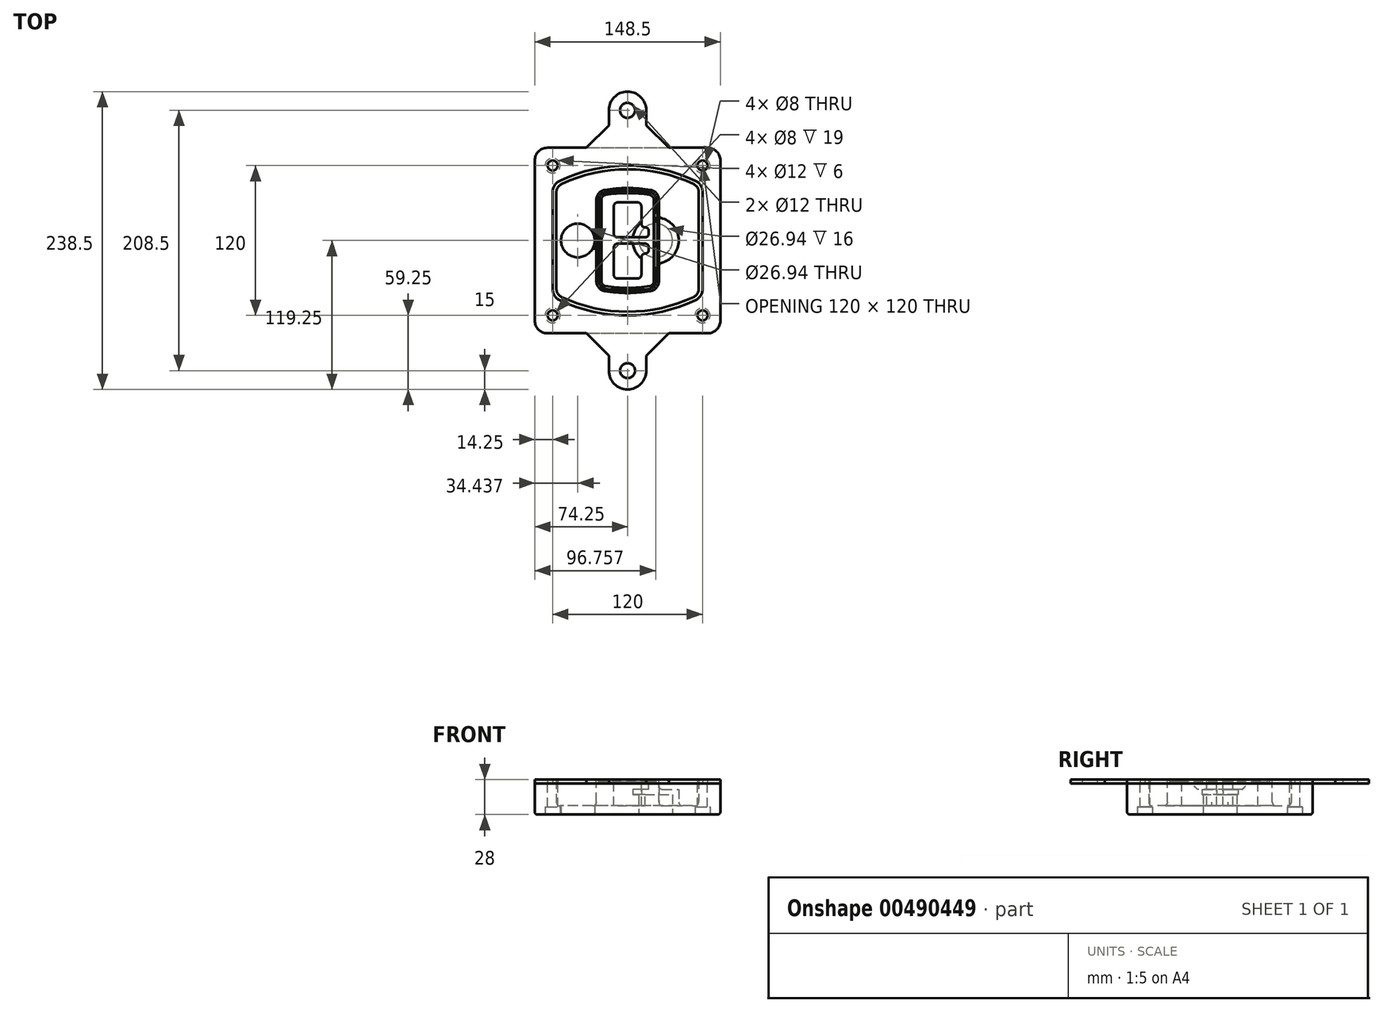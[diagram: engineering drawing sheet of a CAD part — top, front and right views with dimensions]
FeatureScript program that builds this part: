
annotation { "Feature Type Name" : "Feature", "Feature Type Description" : "" }
export const myFeature = defineFeature(function(context is Context, id is Id, definition is map)
    precondition{}
    {
        {
            var Q0;
            Q0=qCreatedBy(makeId("Top.planeOp"),FACE);
            var sketch = newSketch(context, id + "F0", { "sketchPlane" : qUnion([Q0])});
            skPoint(sketch, "E0.rect.middle", {"position": v(0, 0) * mm});
            skLineSegment(sketch, "E1.bottom", {"start": v(-64.25, -74.25) * mm, "end": v(64.25, -74.25) * mm});
            skLineSegment(sketch, "E1.top", {"start": v(-64.25, 74.25) * mm, "end": v(64.25, 74.25) * mm});
            skLineSegment(sketch, "E1.left", {"start": v(-74.25, -64.25) * mm, "end": v(-74.25, 64.25) * mm});
            skLineSegment(sketch, "E1.right", {"start": v(74.25, -64.25) * mm, "end": v(74.25, 64.25) * mm});
            skLineSegment(sketch, "E2", {"start": v(-74.25, 74.25) * mm, "end": v(74.25, -74.25) * mm, "construction": true});
            skLineSegment(sketch, "E3", {"start": v(74.25, 74.25) * mm, "end": v(-74.25, -74.25) * mm, "construction": true});
            skCircle(sketch, "E4", {"center": v(-60, 60) * mm, "radius": 4 * mm});
            skCircle(sketch, "E5", {"center": v(60, 60) * mm, "radius": 4 * mm});
            skCircle(sketch, "E6", {"center": v(60, -60) * mm, "radius": 4 * mm});
            skCircle(sketch, "E7", {"center": v(-60, -60) * mm, "radius": 4 * mm});
            skLineSegment(sketch, "E8", {"start": v(-60, 60) * mm, "end": v(60, 60) * mm, "construction": true});
            skLineSegment(sketch, "E9", {"start": v(60, 60) * mm, "end": v(60, -60) * mm, "construction": true});
            skLineSegment(sketch, "E10", {"start": v(60, -60) * mm, "end": v(-60, -60) * mm, "construction": true});
            skLineSegment(sketch, "E11", {"start": v(-60, -60) * mm, "end": v(-60, 60) * mm, "construction": true});
            skLineSegment(sketch, "E12", {"start": v(-60, 38.83) * mm, "end": v(-60, -38.83) * mm});
            skLineSegment(sketch, "E13", {"start": v(60, 38.83) * mm, "end": v(60, -38.83) * mm});
            skArc(sketch, "E14", {"start": v(54.26, 47.88) * mm, "mid": v(0, 60) * mm, "end": v(-54.26, 47.88) * mm});
            skArc(sketch, "E15", {"start": v(-54.26, -47.88) * mm, "mid": v(0, -60) * mm, "end": v(54.26, -47.88) * mm});
            skLineSegment(sketch, "E16", {"start": v(-60, 0) * mm, "end": v(60, 0) * mm, "construction": true});
            skPoint(sketch, "E17.visualSharp", {"position": v(-60, -45) * mm});
            skArc(sketch, "E17.filletArc", {"start": v(-60, -38.83) * mm, "mid": v(-58.44, -44.2) * mm, "end": v(-54.26, -47.88) * mm});
            skPoint(sketch, "E18.visualSharp", {"position": v(-60, 45) * mm});
            skArc(sketch, "E18.filletArc", {"start": v(-54.26, 47.88) * mm, "mid": v(-58.44, 44.2) * mm, "end": v(-60, 38.83) * mm});
            skPoint(sketch, "E19.visualSharp", {"position": v(60, 45) * mm});
            skArc(sketch, "E19.filletArc", {"start": v(60, 38.83) * mm, "mid": v(58.44, 44.2) * mm, "end": v(54.26, 47.88) * mm});
            skPoint(sketch, "E20.visualSharp", {"position": v(60, -45) * mm});
            skArc(sketch, "E20.filletArc", {"start": v(54.26, -47.88) * mm, "mid": v(58.44, -44.2) * mm, "end": v(60, -38.83) * mm});
            skPoint(sketch, "E21.visualSharp", {"position": v(-74.25, 74.25) * mm});
            skArc(sketch, "E21.filletArc", {"start": v(-64.25, 74.25) * mm, "mid": v(-71.32, 71.32) * mm, "end": v(-74.25, 64.25) * mm});
            skPoint(sketch, "E22.visualSharp", {"position": v(74.25, 74.25) * mm});
            skArc(sketch, "E22.filletArc", {"start": v(74.25, 64.25) * mm, "mid": v(71.32, 71.32) * mm, "end": v(64.25, 74.25) * mm});
            skPoint(sketch, "E23.visualSharp", {"position": v(74.25, -74.25) * mm});
            skArc(sketch, "E23.filletArc", {"start": v(64.25, -74.25) * mm, "mid": v(71.32, -71.32) * mm, "end": v(74.25, -64.25) * mm});
            skPoint(sketch, "E24.visualSharp", {"position": v(-74.25, -74.25) * mm});
            skArc(sketch, "E24.filletArc", {"start": v(-74.25, -64.25) * mm, "mid": v(-71.32, -71.32) * mm, "end": v(-64.25, -74.25) * mm});
            skArc(sketch, "E25.0", {"start": v(57, 38.83) * mm, "mid": v(55.9, 42.58) * mm, "end": v(52.98, 45.17) * mm});
            skLineSegment(sketch, "E25.1", {"start": v(57, 38.83) * mm, "end": v(57, -38.83) * mm});
            skArc(sketch, "E25.2", {"start": v(52.98, -45.17) * mm, "mid": v(55.9, -42.58) * mm, "end": v(57, -38.83) * mm});
            skArc(sketch, "E25.3", {"start": v(-52.98, -45.17) * mm, "mid": v(0, -57) * mm, "end": v(52.98, -45.17) * mm});
            skArc(sketch, "E25.4", {"start": v(-57, -38.83) * mm, "mid": v(-55.9, -42.58) * mm, "end": v(-52.98, -45.17) * mm});
            skArc(sketch, "E25.5", {"start": v(52.98, 45.17) * mm, "mid": v(0, 57) * mm, "end": v(-52.98, 45.17) * mm});
            skLineSegment(sketch, "E25.6", {"start": v(-57, 38.83) * mm, "end": v(-57, -38.83) * mm});
            skArc(sketch, "E25.7", {"start": v(-52.98, 45.17) * mm, "mid": v(-55.9, 42.58) * mm, "end": v(-57, 38.83) * mm});
            skArc(sketch, "E26.0", {"start": v(-55.96, 51.5) * mm, "mid": v(-61.82, 46.33) * mm, "end": v(-64, 38.83) * mm});
            skArc(sketch, "E26.1", {"start": v(55.96, 51.5) * mm, "mid": v(0, 64) * mm, "end": v(-55.96, 51.5) * mm});
            skArc(sketch, "E26.2", {"start": v(64, 38.83) * mm, "mid": v(61.82, 46.33) * mm, "end": v(55.96, 51.5) * mm});
            skLineSegment(sketch, "E26.3", {"start": v(64, 38.83) * mm, "end": v(64, -38.83) * mm});
            skArc(sketch, "E26.4", {"start": v(55.96, -51.5) * mm, "mid": v(61.82, -46.33) * mm, "end": v(64, -38.83) * mm});
            skLineSegment(sketch, "E26.5", {"start": v(-64, 38.83) * mm, "end": v(-64, -38.83) * mm});
            skArc(sketch, "E26.6", {"start": v(-55.96, -51.5) * mm, "mid": v(0, -64) * mm, "end": v(55.96, -51.5) * mm});
            skArc(sketch, "E26.7", {"start": v(-64, -38.83) * mm, "mid": v(-61.82, -46.33) * mm, "end": v(-55.96, -51.5) * mm});
            skSolve(sketch);
        }
        {
            var Q0;
            Q0=makeQuery(id+"F0.imprint","IMPRINT",FACE,{"disambiguationData":[TD([[makeQuery(id+"F0.imprint","IMPRINT",EDGE,{"derivedFrom":sQuery(id+"F0.wireOp",EDGE,"E1.bottom")}),1.0]])]});
            var Q1;
            Q1=makeQuery(id+"F0.imprint","IMPRINT",FACE,{"disambiguationData":[TD([[makeQuery(id+"F0.imprint","IMPRINT",EDGE,{"derivedFrom":sQuery(id+"F0.wireOp",EDGE,"E12")}),1.0]])]});
            var Q2;
            Q2=makeQuery(id+"F0.imprint","IMPRINT",FACE,{"disambiguationData":[TD([[makeQuery(id+"F0.imprint","IMPRINT",EDGE,{"derivedFrom":sQuery(id+"F0.wireOp",EDGE,"E25.0")}),1.0]])]});
            var Q3;
            Q3=makeQuery(id+"F0.imprint","IMPRINT",FACE,{"disambiguationData":[TD([[makeQuery(id+"F0.imprint","IMPRINT",EDGE,{"derivedFrom":sQuery(id+"F0.wireOp",EDGE,"E12")}),-1.0]])]});
            extrude(context, id + "F1", {"entities" : qUnion([Q0, Q1, Q2, Q3]), "oppositeDirection" : true, "depth" : 25 * mm});
        }
        {
            var Q0;
            Q0=makeQuery(id+"F0.imprint","IMPRINT",FACE,{"disambiguationData":[TD([[makeQuery(id+"F0.imprint","IMPRINT",EDGE,{"derivedFrom":sQuery(id+"F0.wireOp",EDGE,"E12")}),1.0]])]});
            extrude(context, id + "F2", {"entities" : qUnion([Q0]), "operationType" : NewBodyOperationType.ADD, "depth" : 3 * mm});
        }
        {
            var Q0;
            Q0=makeQuery(id+"F0.imprint","IMPRINT",FACE,{"disambiguationData":[TD([[makeQuery(id+"F0.imprint","IMPRINT",EDGE,{"derivedFrom":sQuery(id+"F0.wireOp",EDGE,"E25.0")}),1.0]])]});
            extrude(context, id + "F3", {"entities" : qUnion([Q0]), "operationType" : NewBodyOperationType.REMOVE, "oppositeDirection" : true, "depth" : 18 * mm});
        }
        {
            var Q0;
            Q0=makeQuery(id+"F2.opExtrude","CAP_FACE",FACE,{"disambiguationData":[OSD([sQuery(id+"F0.wireOp",EDGE,"E12"),sQuery(id+"F0.wireOp",EDGE,"E13"),sQuery(id+"F0.wireOp",EDGE,"E14"),sQuery(id+"F0.wireOp",EDGE,"E15"),sQuery(id+"F0.wireOp",EDGE,"E17.filletArc"),sQuery(id+"F0.wireOp",EDGE,"E18.filletArc"),sQuery(id+"F0.wireOp",EDGE,"E19.filletArc"),sQuery(id+"F0.wireOp",EDGE,"E20.filletArc"),sQuery(id+"F0.wireOp",EDGE,"E25.0"),sQuery(id+"F0.wireOp",EDGE,"E25.1"),sQuery(id+"F0.wireOp",EDGE,"E25.2"),sQuery(id+"F0.wireOp",EDGE,"E25.3"),sQuery(id+"F0.wireOp",EDGE,"E25.4"),sQuery(id+"F0.wireOp",EDGE,"E25.5"),sQuery(id+"F0.wireOp",EDGE,"E25.6"),sQuery(id+"F0.wireOp",EDGE,"E25.7")])],"isStart":false});
            var sketch = newSketch(context, id + "F4", { "sketchPlane" : qUnion([Q0])});
            skArc(sketch, "E27.0", {"start": v(-18.34, -40.45) * mm, "mid": v(0, -42) * mm, "end": v(18.34, -40.45) * mm});
            skArc(sketch, "E28.0", {"start": v(18.34, 40.45) * mm, "mid": v(0, 42) * mm, "end": v(-18.34, 40.45) * mm});
            skLineSegment(sketch, "E29", {"start": v(-25, 32.57) * mm, "end": v(-25, -32.57) * mm});
            skLineSegment(sketch, "E30", {"start": v(25, 32.57) * mm, "end": v(25, -32.57) * mm});
            skLineSegment(sketch, "E31", {"start": v(-25, 39.1) * mm, "end": v(25, 39.1) * mm, "construction": true});
            skLineSegment(sketch, "E32", {"start": v(-25, -39.1) * mm, "end": v(25, -39.1) * mm, "construction": true});
            skPoint(sketch, "E33.visualSharp", {"position": v(-25, 39.1) * mm});
            skArc(sketch, "E33.filletArc", {"start": v(-18.34, 40.45) * mm, "mid": v(-23.11, 37.73) * mm, "end": v(-25, 32.57) * mm});
            skPoint(sketch, "E34.visualSharp", {"position": v(25, 39.1) * mm});
            skArc(sketch, "E34.filletArc", {"start": v(25, 32.57) * mm, "mid": v(23.11, 37.73) * mm, "end": v(18.34, 40.45) * mm});
            skPoint(sketch, "E35.visualSharp", {"position": v(25, -39.1) * mm});
            skArc(sketch, "E35.filletArc", {"start": v(18.34, -40.45) * mm, "mid": v(23.11, -37.73) * mm, "end": v(25, -32.57) * mm});
            skPoint(sketch, "E36.visualSharp", {"position": v(-25, -39.1) * mm});
            skArc(sketch, "E36.filletArc", {"start": v(-25, -32.57) * mm, "mid": v(-23.11, -37.73) * mm, "end": v(-18.34, -40.45) * mm});
            skArc(sketch, "E37.0", {"start": v(52.98, 45.17) * mm, "mid": v(0, 57) * mm, "end": v(-52.98, 45.17) * mm});
            skArc(sketch, "E37.1", {"start": v(-52.98, 45.17) * mm, "mid": v(-55.9, 42.58) * mm, "end": v(-57, 38.83) * mm});
            skLineSegment(sketch, "E37.2", {"start": v(-57, 38.83) * mm, "end": v(-57, -38.83) * mm});
            skArc(sketch, "E37.3", {"start": v(-57, -38.83) * mm, "mid": v(-55.9, -42.58) * mm, "end": v(-52.98, -45.17) * mm});
            skArc(sketch, "E37.4", {"start": v(-52.98, -45.17) * mm, "mid": v(0, -57) * mm, "end": v(52.98, -45.17) * mm});
            skArc(sketch, "E37.5", {"start": v(52.98, -45.17) * mm, "mid": v(55.9, -42.58) * mm, "end": v(57, -38.83) * mm});
            skLineSegment(sketch, "E37.6", {"start": v(57, 38.83) * mm, "end": v(57, -38.83) * mm});
            skArc(sketch, "E37.7", {"start": v(57, 38.83) * mm, "mid": v(55.9, 42.58) * mm, "end": v(52.98, 45.17) * mm});
            skLineSegment(sketch, "E38.0", {"start": v(23, 32.57) * mm, "end": v(23, -32.57) * mm});
            skArc(sketch, "E38.1", {"start": v(18, -38.48) * mm, "mid": v(21.58, -36.44) * mm, "end": v(23, -32.57) * mm});
            skArc(sketch, "E38.2", {"start": v(-18, -38.48) * mm, "mid": v(0, -40) * mm, "end": v(18, -38.48) * mm});
            skArc(sketch, "E38.3", {"start": v(-23, -32.57) * mm, "mid": v(-21.58, -36.44) * mm, "end": v(-18, -38.48) * mm});
            skLineSegment(sketch, "E38.4", {"start": v(-23, 32.57) * mm, "end": v(-23, -32.57) * mm});
            skArc(sketch, "E38.5", {"start": v(23, 32.57) * mm, "mid": v(21.58, 36.44) * mm, "end": v(18, 38.48) * mm});
            skArc(sketch, "E38.6", {"start": v(-18, 38.48) * mm, "mid": v(-21.58, 36.44) * mm, "end": v(-23, 32.57) * mm});
            skArc(sketch, "E38.7", {"start": v(18, 38.48) * mm, "mid": v(0, 40) * mm, "end": v(-18, 38.48) * mm});
            skArc(sketch, "E39.0", {"start": v(21, 32.57) * mm, "mid": v(20.06, 35.15) * mm, "end": v(17.67, 36.5) * mm});
            skLineSegment(sketch, "E39.1", {"start": v(21, 32.57) * mm, "end": v(21, -32.57) * mm});
            skArc(sketch, "E39.2", {"start": v(17.67, -36.5) * mm, "mid": v(20.06, -35.15) * mm, "end": v(21, -32.57) * mm});
            skArc(sketch, "E39.3", {"start": v(-17.67, -36.5) * mm, "mid": v(0, -38) * mm, "end": v(17.67, -36.5) * mm});
            skArc(sketch, "E39.4", {"start": v(-21, -32.57) * mm, "mid": v(-20.06, -35.15) * mm, "end": v(-17.67, -36.5) * mm});
            skArc(sketch, "E39.5", {"start": v(17.67, 36.5) * mm, "mid": v(0, 38) * mm, "end": v(-17.67, 36.5) * mm});
            skLineSegment(sketch, "E39.6", {"start": v(-21, 32.57) * mm, "end": v(-21, -32.57) * mm});
            skArc(sketch, "E39.7", {"start": v(-17.67, 36.5) * mm, "mid": v(-20.06, 35.15) * mm, "end": v(-21, 32.57) * mm});
            skLineSegment(sketch, "E40", {"start": v(-25, 0) * mm, "end": v(25, 0) * mm, "construction": true});
            skLineSegment(sketch, "E41", {"start": v(-11, 5.5) * mm, "end": v(-11, 27.5) * mm});
            skLineSegment(sketch, "E42", {"start": v(-8, 30.5) * mm, "end": v(8, 30.5) * mm});
            skLineSegment(sketch, "E43", {"start": v(11, 27.5) * mm, "end": v(11, 13.5) * mm});
            skLineSegment(sketch, "E44", {"start": v(14, 10.5) * mm, "end": v(14, 10.5) * mm});
            skLineSegment(sketch, "E45", {"start": v(17, 7.5) * mm, "end": v(17, 5.5) * mm});
            skLineSegment(sketch, "E46", {"start": v(14, 2.5) * mm, "end": v(-8, 2.5) * mm});
            skPoint(sketch, "E47.visualSharp", {"position": v(-11, 30.5) * mm});
            skArc(sketch, "E47.filletArc", {"start": v(-8, 30.5) * mm, "mid": v(-10.12, 29.62) * mm, "end": v(-11, 27.5) * mm});
            skPoint(sketch, "E48.visualSharp", {"position": v(11, 30.5) * mm});
            skArc(sketch, "E48.filletArc", {"start": v(11, 27.5) * mm, "mid": v(10.12, 29.62) * mm, "end": v(8, 30.5) * mm});
            skPoint(sketch, "E49.visualSharp", {"position": v(11, 10.5) * mm});
            skArc(sketch, "E49.filletArc", {"start": v(11, 13.5) * mm, "mid": v(11.88, 11.38) * mm, "end": v(14, 10.5) * mm});
            skPoint(sketch, "E50.visualSharp", {"position": v(17, 10.5) * mm});
            skArc(sketch, "E50.filletArc", {"start": v(17, 7.5) * mm, "mid": v(16.12, 9.62) * mm, "end": v(14, 10.5) * mm});
            skPoint(sketch, "E51.visualSharp", {"position": v(17, 2.5) * mm});
            skArc(sketch, "E51.filletArc", {"start": v(14, 2.5) * mm, "mid": v(16.12, 3.38) * mm, "end": v(17, 5.5) * mm});
            skPoint(sketch, "E52.visualSharp", {"position": v(-11, 2.5) * mm});
            skArc(sketch, "E52.filletArc", {"start": v(-11, 5.5) * mm, "mid": v(-10.12, 3.38) * mm, "end": v(-8, 2.5) * mm});
            skLineSegment(sketch, "E53.0.MirrorCS", {"start": v(14, -2.5) * mm, "end": v(-8, -2.5) * mm});
            skArc(sketch, "E54.0.MirrorCS", {"start": v(-11, -5.5) * mm, "mid": v(-10.12, -3.38) * mm, "end": v(-8, -2.5) * mm});
            skLineSegment(sketch, "E55.0.MirrorCS", {"start": v(-11, -5.5) * mm, "end": v(-11, -27.5) * mm});
            skArc(sketch, "E56.0.MirrorCS", {"start": v(-8, -30.5) * mm, "mid": v(-10.12, -29.62) * mm, "end": v(-11, -27.5) * mm});
            skLineSegment(sketch, "E57.0.MirrorCS", {"start": v(-8, -30.5) * mm, "end": v(8, -30.5) * mm});
            skArc(sketch, "E58.0.MirrorCS", {"start": v(11, -27.5) * mm, "mid": v(10.12, -29.62) * mm, "end": v(8, -30.5) * mm});
            skLineSegment(sketch, "E59.0.MirrorCS", {"start": v(11, -27.5) * mm, "end": v(11, -13.5) * mm});
            skArc(sketch, "E60.0.MirrorCS", {"start": v(11, -13.5) * mm, "mid": v(11.88, -11.38) * mm, "end": v(14, -10.5) * mm});
            skArc(sketch, "E61.0.MirrorCS", {"start": v(17, -7.5) * mm, "mid": v(16.12, -9.62) * mm, "end": v(14, -10.5) * mm});
            skLineSegment(sketch, "E62.0.MirrorCS", {"start": v(17, -7.5) * mm, "end": v(17, -5.5) * mm});
            skArc(sketch, "E63.0.MirrorCS", {"start": v(14, -2.5) * mm, "mid": v(16.12, -3.38) * mm, "end": v(17, -5.5) * mm});
            skSolve(sketch);
        }
        {
            var Q0;
            Q0=makeQuery(id+"F4.imprint","IMPRINT",FACE,{"disambiguationData":[TD([[makeQuery(id+"F4.imprint","IMPRINT",EDGE,{"derivedFrom":sQuery(id+"F4.wireOp",EDGE,"E27.0")}),1.0]])]});
            var Q1;
            Q1=makeQuery(id+"F4.imprint","IMPRINT",FACE,{"disambiguationData":[TD([[makeQuery(id+"F4.imprint","IMPRINT",EDGE,{"derivedFrom":sQuery(id+"F4.wireOp",EDGE,"E38.0")}),-1.0]])]});
            var Q2;
            Q2=makeQuery(id+"F4.imprint","IMPRINT",FACE,{"disambiguationData":[TD([[makeQuery(id+"F4.imprint","IMPRINT",EDGE,{"derivedFrom":sQuery(id+"F4.wireOp",EDGE,"E39.0")}),1.0]])]});
            extrude(context, id + "F5", {"entities" : qUnion([Q0, Q1, Q2]), "operationType" : NewBodyOperationType.ADD, "endBound" : BoundingType.UP_TO_NEXT, "oppositeDirection" : true, "depth" : 25 * mm});
        }
        {
            var Q0;
            Q0=makeQuery(id+"F4.imprint","IMPRINT",FACE,{"disambiguationData":[TD([[makeQuery(id+"F4.imprint","IMPRINT",EDGE,{"derivedFrom":sQuery(id+"F4.wireOp",EDGE,"E38.0")}),-1.0]])]});
            extrude(context, id + "F6", {"entities" : qUnion([Q0]), "operationType" : NewBodyOperationType.REMOVE, "oppositeDirection" : true, "depth" : 2 * mm});
        }
        {
            var Q0;
            Q0=makeQuery(id+"F1.opExtrude","CAP_FACE",FACE,{"disambiguationData":[OSD([sQuery(id+"F0.wireOp",EDGE,"E1.bottom"),sQuery(id+"F0.wireOp",EDGE,"E1.top"),sQuery(id+"F0.wireOp",EDGE,"E1.left"),sQuery(id+"F0.wireOp",EDGE,"E1.right"),sQuery(id+"F0.wireOp",EDGE,"E4"),sQuery(id+"F0.wireOp",EDGE,"E5"),sQuery(id+"F0.wireOp",EDGE,"E6"),sQuery(id+"F0.wireOp",EDGE,"E7"),sQuery(id+"F0.wireOp",EDGE,"E21.filletArc"),sQuery(id+"F0.wireOp",EDGE,"E22.filletArc"),sQuery(id+"F0.wireOp",EDGE,"E23.filletArc"),sQuery(id+"F0.wireOp",EDGE,"E24.filletArc")])],"isStart":false});
            var sketch = newSketch(context, id + "F7", { "sketchPlane" : qUnion([Q0])});
            skCircle(sketch, "E64", {"center": v(22.5, 0) * mm, "radius": 13.47 * mm});
            skCircle(sketch, "E65", {"center": v(-39.81, 0) * mm, "radius": 13.47 * mm});
            skLineSegment(sketch, "E66", {"start": v(74.25, 0) * mm, "end": v(-74.25, 0) * mm});
            skCircle(sketch, "E67", {"center": v(22.5, 0) * mm, "radius": 18.47 * mm});
            skCircle(sketch, "E68", {"center": v(60, -60) * mm, "radius": 6 * mm});
            skCircle(sketch, "E69", {"center": v(-60, -60) * mm, "radius": 6 * mm});
            skCircle(sketch, "E70", {"center": v(-60, 60) * mm, "radius": 6 * mm});
            skCircle(sketch, "E71", {"center": v(60, 60) * mm, "radius": 6 * mm});
            skSolve(sketch);
        }
        {
            var Q0;
            {var subQ1=sQuery(id+"F7.wireOp",EDGE,"E66");var subQ4=sQuery(id+"F7.wireOp",EDGE,"E64");var subQ6=makeQuery(id+"F7.imprint","INTERSECT",VERTEX,{"disambiguationData":[OD(0.0)],"derivedFrom":[subQ4,subQ1]});Q0=makeQuery(id+"F7.imprint","IMPRINT",FACE,{"disambiguationData":[TD([[makeQuery(id+"F7.imprint","IMPRINT",EDGE,{"disambiguationData":[TD([[subQ6,-1.0]])],"derivedFrom":subQ4}),-1.0]])]});}
            var Q1;
            {var subQ0=sQuery(id+"F7.wireOp",EDGE,"E66");var subQ1=sQuery(id+"F7.wireOp",EDGE,"E64");var subQ3=makeQuery(id+"F7.imprint","INTERSECT",VERTEX,{"disambiguationData":[OD(0.0)],"derivedFrom":[subQ1,subQ0]});Q1=makeQuery(id+"F7.imprint","IMPRINT",FACE,{"disambiguationData":[TD([[makeQuery(id+"F7.imprint","IMPRINT",EDGE,{"disambiguationData":[TD([[subQ3,-1.0]])],"derivedFrom":subQ1}),1.0]])]});}
            var Q2;
            {var subQ0=sQuery(id+"F7.wireOp",EDGE,"E66");var subQ1=sQuery(id+"F7.wireOp",EDGE,"E64");var subQ3=makeQuery(id+"F7.imprint","INTERSECT",VERTEX,{"disambiguationData":[OD(0.0)],"derivedFrom":[subQ1,subQ0]});Q2=makeQuery(id+"F7.imprint","IMPRINT",FACE,{"disambiguationData":[TD([[makeQuery(id+"F7.imprint","IMPRINT",EDGE,{"disambiguationData":[TD([[subQ3,1.0]])],"derivedFrom":subQ1}),1.0]])]});}
            var Q3;
            {var subQ1=sQuery(id+"F7.wireOp",EDGE,"E66");var subQ4=sQuery(id+"F7.wireOp",EDGE,"E64");var subQ6=makeQuery(id+"F7.imprint","INTERSECT",VERTEX,{"disambiguationData":[OD(0.0)],"derivedFrom":[subQ4,subQ1]});Q3=makeQuery(id+"F7.imprint","IMPRINT",FACE,{"disambiguationData":[TD([[makeQuery(id+"F7.imprint","IMPRINT",EDGE,{"disambiguationData":[TD([[subQ6,1.0]])],"derivedFrom":subQ4}),-1.0]])]});}
            extrude(context, id + "F8", {"entities" : qUnion([Q0, Q1, Q2, Q3]), "operationType" : NewBodyOperationType.ADD, "oppositeDirection" : true, "depth" : 20 * mm});
        }
        {
            var Q0;
            {var subQ0=sQuery(id+"F7.wireOp",EDGE,"E66");var subQ1=sQuery(id+"F7.wireOp",EDGE,"E64");var subQ3=makeQuery(id+"F7.imprint","INTERSECT",VERTEX,{"disambiguationData":[OD(0.0)],"derivedFrom":[subQ1,subQ0]});Q0=makeQuery(id+"F7.imprint","IMPRINT",FACE,{"disambiguationData":[TD([[makeQuery(id+"F7.imprint","IMPRINT",EDGE,{"disambiguationData":[TD([[subQ3,-1.0]])],"derivedFrom":subQ1}),1.0]])]});}
            var Q1;
            {var subQ0=sQuery(id+"F7.wireOp",EDGE,"E66");var subQ1=sQuery(id+"F7.wireOp",EDGE,"E64");var subQ3=makeQuery(id+"F7.imprint","INTERSECT",VERTEX,{"disambiguationData":[OD(0.0)],"derivedFrom":[subQ1,subQ0]});Q1=makeQuery(id+"F7.imprint","IMPRINT",FACE,{"disambiguationData":[TD([[makeQuery(id+"F7.imprint","IMPRINT",EDGE,{"disambiguationData":[TD([[subQ3,1.0]])],"derivedFrom":subQ1}),1.0]])]});}
            extrude(context, id + "F9", {"entities" : qUnion([Q0, Q1]), "operationType" : NewBodyOperationType.REMOVE, "oppositeDirection" : true, "depth" : 16 * mm});
        }
        {
            var Q0;
            {var subQ0=sQuery(id+"F7.wireOp",EDGE,"E66");var subQ1=sQuery(id+"F7.wireOp",EDGE,"E65");var subQ3=makeQuery(id+"F7.imprint","INTERSECT",VERTEX,{"disambiguationData":[OD(0.0)],"derivedFrom":[subQ1,subQ0]});Q0=makeQuery(id+"F7.imprint","IMPRINT",FACE,{"disambiguationData":[TD([[makeQuery(id+"F7.imprint","IMPRINT",EDGE,{"disambiguationData":[TD([[subQ3,-1.0]])],"derivedFrom":subQ1}),1.0]])]});}
            var Q1;
            {var subQ0=sQuery(id+"F7.wireOp",EDGE,"E66");var subQ1=sQuery(id+"F7.wireOp",EDGE,"E65");var subQ3=makeQuery(id+"F7.imprint","INTERSECT",VERTEX,{"disambiguationData":[OD(0.0)],"derivedFrom":[subQ1,subQ0]});Q1=makeQuery(id+"F7.imprint","IMPRINT",FACE,{"disambiguationData":[TD([[makeQuery(id+"F7.imprint","IMPRINT",EDGE,{"disambiguationData":[TD([[subQ3,1.0]])],"derivedFrom":subQ1}),1.0]])]});}
            extrude(context, id + "F10", {"entities" : qUnion([Q0, Q1]), "operationType" : NewBodyOperationType.REMOVE, "oppositeDirection" : true, "depth" : 25 * mm});
        }
        {
            var Q0;
            Q0=makeQuery(id+"F7.imprint","IMPRINT",FACE,{"disambiguationData":[TD([[makeQuery(id+"F7.imprint","IMPRINT",EDGE,{"derivedFrom":sQuery(id+"F7.wireOp",EDGE,"E68")}),1.0]])]});
            var Q1;
            Q1=makeQuery(id+"F7.imprint","IMPRINT",FACE,{"disambiguationData":[TD([[makeQuery(id+"F7.imprint","IMPRINT",EDGE,{"derivedFrom":makeQuery(id+"F1.opExtrude","CAP_EDGE",EDGE,{"disambiguationData":[OSD([sQuery(id+"F0.wireOp",EDGE,"E5")])],"isStart":false})}),-1.0]])]});
            var Q2;
            Q2=makeQuery(id+"F7.imprint","IMPRINT",FACE,{"disambiguationData":[TD([[makeQuery(id+"F7.imprint","IMPRINT",EDGE,{"derivedFrom":sQuery(id+"F7.wireOp",EDGE,"E69")}),1.0]])]});
            var Q3;
            Q3=makeQuery(id+"F7.imprint","IMPRINT",FACE,{"disambiguationData":[TD([[makeQuery(id+"F7.imprint","IMPRINT",EDGE,{"derivedFrom":makeQuery(id+"F1.opExtrude","CAP_EDGE",EDGE,{"disambiguationData":[OSD([sQuery(id+"F0.wireOp",EDGE,"E4")])],"isStart":false})}),-1.0]])]});
            var Q4;
            Q4=makeQuery(id+"F7.imprint","IMPRINT",FACE,{"disambiguationData":[TD([[makeQuery(id+"F7.imprint","IMPRINT",EDGE,{"derivedFrom":sQuery(id+"F7.wireOp",EDGE,"E70")}),1.0]])]});
            var Q5;
            Q5=makeQuery(id+"F7.imprint","IMPRINT",FACE,{"disambiguationData":[TD([[makeQuery(id+"F7.imprint","IMPRINT",EDGE,{"derivedFrom":makeQuery(id+"F1.opExtrude","CAP_EDGE",EDGE,{"disambiguationData":[OSD([sQuery(id+"F0.wireOp",EDGE,"E7")])],"isStart":false})}),-1.0]])]});
            var Q6;
            Q6=makeQuery(id+"F7.imprint","IMPRINT",FACE,{"disambiguationData":[TD([[makeQuery(id+"F7.imprint","IMPRINT",EDGE,{"derivedFrom":sQuery(id+"F7.wireOp",EDGE,"E71")}),1.0]])]});
            var Q7;
            Q7=makeQuery(id+"F7.imprint","IMPRINT",FACE,{"disambiguationData":[TD([[makeQuery(id+"F7.imprint","IMPRINT",EDGE,{"derivedFrom":makeQuery(id+"F1.opExtrude","CAP_EDGE",EDGE,{"disambiguationData":[OSD([sQuery(id+"F0.wireOp",EDGE,"E6")])],"isStart":false})}),-1.0]])]});
            extrude(context, id + "F11", {"entities" : qUnion([Q0, Q1, Q2, Q3, Q4, Q5, Q6, Q7]), "operationType" : NewBodyOperationType.REMOVE, "oppositeDirection" : true, "depth" : 6 * mm});
        }
        {
            var Q0;
            Q0=makeQuery(id+"F9.boolean.opBoolean","COPY",FACE,{"derivedFrom":makeQuery(id+"F9.opExtrude","CAP_FACE",FACE,{"disambiguationData":[OSD([sQuery(id+"F7.wireOp",EDGE,"E64")])],"isStart":false})});
            var sketch = newSketch(context, id + "F12", { "sketchPlane" : qUnion([Q0])});
            skArc(sketch, "E72.0", {"start": v(11, 14.45) * mm, "mid": v(6.45, 9.13) * mm, "end": v(4.2, 2.5) * mm});
            skArc(sketch, "E72.1", {"start": v(4.2, -2.5) * mm, "mid": v(6.45, -9.13) * mm, "end": v(11, -14.45) * mm});
            skLineSegment(sketch, "E73", {"start": v(4.2, -2.5) * mm, "end": v(14, -2.5) * mm});
            skLineSegment(sketch, "E74.0", {"start": v(14, 2.5) * mm, "end": v(4.2, 2.5) * mm});
            skArc(sketch, "E74.1", {"start": v(14, 2.5) * mm, "mid": v(16.12, 3.38) * mm, "end": v(17, 5.5) * mm});
            skLineSegment(sketch, "E74.2", {"start": v(17, 7.5) * mm, "end": v(17, 5.5) * mm});
            skArc(sketch, "E74.3", {"start": v(17, 7.5) * mm, "mid": v(16.12, 9.62) * mm, "end": v(14, 10.5) * mm});
            skArc(sketch, "E74.4", {"start": v(11, 13.5) * mm, "mid": v(11.88, 11.38) * mm, "end": v(14, 10.5) * mm});
            skLineSegment(sketch, "E74.5", {"start": v(11, 14.45) * mm, "end": v(11, 13.5) * mm});
            skLineSegment(sketch, "E74.7", {"start": v(14, -2.5) * mm, "end": v(4.2, -2.5) * mm});
            skArc(sketch, "E74.8", {"start": v(14, -2.5) * mm, "mid": v(16.12, -3.38) * mm, "end": v(17, -5.5) * mm});
            skLineSegment(sketch, "E74.9", {"start": v(17, -7.5) * mm, "end": v(17, -5.5) * mm});
            skArc(sketch, "E74.10", {"start": v(17, -7.5) * mm, "mid": v(16.12, -9.62) * mm, "end": v(14, -10.5) * mm});
            skArc(sketch, "E74.11", {"start": v(11, -13.5) * mm, "mid": v(11.88, -11.38) * mm, "end": v(14, -10.5) * mm});
            skLineSegment(sketch, "E74.12", {"start": v(11, -14.45) * mm, "end": v(11, -13.5) * mm});
            skPoint(sketch, "E75.orphan", {"position": v(11, -27.5) * mm});
            skPoint(sketch, "E76.orphan", {"position": v(-8, -2.5) * mm});
            skPoint(sketch, "E77.orphan", {"position": v(-8, 2.5) * mm});
            skPoint(sketch, "E78.orphan", {"position": v(11, 27.5) * mm});
            skSolve(sketch);
        }
        {
            var Q0;
            {var subQ7=sQuery(id+"F12.wireOp",EDGE,"E72.0");var subQ14=sQuery(id+"F12.wireOp",EDGE,"E72.1");var subQ16=sQuery(id+"F12.wireOp",EDGE,"E74.1");var subQ18=sQuery(id+"F12.wireOp",EDGE,"E74.8");Q0=qUnion([makeQuery(id+"F12.imprint","IMPRINT",FACE,{"disambiguationData":[TD([[makeQuery(id+"F12.imprint","IMPRINT",EDGE,{"derivedFrom":subQ7}),1.0]])]}),makeQuery(id+"F12.imprint","IMPRINT",FACE,{"disambiguationData":[TD([[makeQuery(id+"F12.imprint","IMPRINT",EDGE,{"derivedFrom":subQ14}),1.0]])]}),makeQuery(id+"F12.imprint","IMPRINT",FACE,{"disambiguationData":[TD([[makeQuery(id+"F12.imprint","IMPRINT",EDGE,{"derivedFrom":subQ16}),1.0]])]}),makeQuery(id+"F12.imprint","IMPRINT",FACE,{"disambiguationData":[TD([[makeQuery(id+"F12.imprint","IMPRINT",EDGE,{"derivedFrom":subQ18}),-1.0]])]})]);}
            var Q1;
            Q1=makeQuery(id+"F5.boolean.opBoolean","SPLIT",FACE,{"disambiguationData":[TD([makeQuery(id+"F5.opExtrude","SWEPT_FACE",FACE,{"disambiguationData":[OSD([sQuery(id+"F4.wireOp",EDGE,"E41")])]})])],"derivedFrom":makeQuery(id+"F3.boolean.opBoolean","COPY",FACE,{"derivedFrom":makeQuery(id+"F3.opExtrude","CAP_FACE",FACE,{"disambiguationData":[OSD([sQuery(id+"F0.wireOp",EDGE,"E25.0"),sQuery(id+"F0.wireOp",EDGE,"E25.1"),sQuery(id+"F0.wireOp",EDGE,"E25.2"),sQuery(id+"F0.wireOp",EDGE,"E25.3"),sQuery(id+"F0.wireOp",EDGE,"E25.4"),sQuery(id+"F0.wireOp",EDGE,"E25.5"),sQuery(id+"F0.wireOp",EDGE,"E25.6"),sQuery(id+"F0.wireOp",EDGE,"E25.7")])],"isStart":false})})});
            extrude(context, id + "F13", {"entities" : qUnion([Q0]), "operationType" : NewBodyOperationType.REMOVE, "endBound" : BoundingType.UP_TO_SURFACE, "endBoundEntityFace" : qUnion([Q1]), "depth" : 25 * mm});
        }
        {
            var Q0;
            Q0=makeQuery(id+"F3.boolean.opBoolean","COPY",EDGE,{"derivedFrom":makeQuery(id+"F3.opExtrude","CAP_EDGE",EDGE,{"disambiguationData":[OSD([sQuery(id+"F0.wireOp",EDGE,"E25.6")])],"isStart":false})});
            var Q1;
            Q1=makeQuery(id+"F8.boolean.opBoolean","INTERSECT",EDGE,{"derivedFrom":[makeQuery(id+"F5.opExtrude","SWEPT_FACE",FACE,{"disambiguationData":[OSD([sQuery(id+"F4.wireOp",EDGE,"E30")])]}),makeQuery(id+"F8.opExtrude","CAP_FACE",FACE,{"disambiguationData":[OSD([sQuery(id+"F7.wireOp",EDGE,"E67")])],"isStart":false})]});
            var Q2;
            Q2=makeQuery(id+"F8.boolean.opBoolean","INTERSECT",EDGE,{"disambiguationData":[OD(1.0)],"derivedFrom":[makeQuery(id+"F5.opExtrude","SWEPT_FACE",FACE,{"disambiguationData":[OSD([sQuery(id+"F4.wireOp",EDGE,"E30")])]}),makeQuery(id+"F8.opExtrude","SWEPT_FACE",FACE,{"disambiguationData":[OSD([sQuery(id+"F7.wireOp",EDGE,"E67")])]})]});
            var Q3;
            {var subQ0=sQuery(id+"F4.wireOp",EDGE,"E30");Q3=makeQuery(id+"F8.boolean.opBoolean","SPLIT",EDGE,{"disambiguationData":[TD([makeQuery(id+"F5.opExtrude","SWEPT_FACE",FACE,{"disambiguationData":[OSD([sQuery(id+"F4.wireOp",EDGE,"E35.filletArc")])]})])],"derivedFrom":makeQuery(id+"F5.opExtrude","CAP_EDGE",EDGE,{"disambiguationData":[OSD([subQ0])],"isStart":false})});}
            var Q4;
            {var subQ0=sQuery(id+"F0.wireOp",EDGE,"E25.7");var subQ1=sQuery(id+"F0.wireOp",EDGE,"E25.1");var subQ2=sQuery(id+"F0.wireOp",EDGE,"E25.6");var subQ3=sQuery(id+"F0.wireOp",EDGE,"E25.5");var subQ4=sQuery(id+"F0.wireOp",EDGE,"E25.4");var subQ5=sQuery(id+"F0.wireOp",EDGE,"E25.0");var subQ6=sQuery(id+"F0.wireOp",EDGE,"E25.2");var subQ7=sQuery(id+"F0.wireOp",EDGE,"E25.3");Q4=makeQuery(id+"F8.boolean.opBoolean","INTERSECT",EDGE,{"derivedFrom":[makeQuery(id+"F5.boolean.opBoolean","SPLIT",FACE,{"disambiguationData":[TD([makeQuery(id+"F2.opExtrude","SWEPT_FACE",FACE,{"disambiguationData":[OSD([subQ5])]})])],"derivedFrom":makeQuery(id+"F3.boolean.opBoolean","COPY",FACE,{"derivedFrom":makeQuery(id+"F3.opExtrude","CAP_FACE",FACE,{"disambiguationData":[OSD([subQ5,subQ1,subQ6,subQ7,subQ4,subQ3,subQ2,subQ0])],"isStart":false})})}),makeQuery(id+"F8.opExtrude","SWEPT_FACE",FACE,{"disambiguationData":[OSD([sQuery(id+"F7.wireOp",EDGE,"E67")])]})]});}
            var Q5;
            Q5=makeQuery(id+"F8.boolean.opBoolean","INTERSECT",EDGE,{"disambiguationData":[OD(0.0)],"derivedFrom":[makeQuery(id+"F5.opExtrude","SWEPT_FACE",FACE,{"disambiguationData":[OSD([sQuery(id+"F4.wireOp",EDGE,"E30")])]}),makeQuery(id+"F8.opExtrude","SWEPT_FACE",FACE,{"disambiguationData":[OSD([sQuery(id+"F7.wireOp",EDGE,"E67")])]})]});
            fillet(context, id + "F14", {"entities" : qUnion([Q0, Q1, Q2, Q3, Q4, Q5]), "radius" : 3 * mm, "tangentPropagation" : true, "allowEdgeOverflow" : false});
        }
        {
            var Q0;
            Q0=makeQuery(id+"F1.opExtrude","CAP_EDGE",EDGE,{"disambiguationData":[OSD([sQuery(id+"F0.wireOp",EDGE,"E1.bottom")])],"isStart":false});
            fillet(context, id + "F15", {"entities" : qUnion([Q0]), "radius" : 2 * mm, "tangentPropagation" : true, "allowEdgeOverflow" : false});
        }
        {
            var Q0;
            {var subQ0=sQuery(id+"F0.wireOp",EDGE,"E21.filletArc");var subQ1=sQuery(id+"F0.wireOp",EDGE,"E7");var subQ2=sQuery(id+"F0.wireOp",EDGE,"E6");var subQ3=sQuery(id+"F0.wireOp",EDGE,"E5");var subQ4=sQuery(id+"F0.wireOp",EDGE,"E4");var subQ5=sQuery(id+"F0.wireOp",EDGE,"E22.filletArc");var subQ6=sQuery(id+"F0.wireOp",EDGE,"E1.bottom");var subQ7=sQuery(id+"F0.wireOp",EDGE,"E1.right");var subQ8=sQuery(id+"F0.wireOp",EDGE,"E1.top");var subQ9=sQuery(id+"F0.wireOp",EDGE,"E1.left");var subQ10=sQuery(id+"F0.wireOp",EDGE,"E23.filletArc");var subQ11=sQuery(id+"F0.wireOp",EDGE,"E24.filletArc");Q0=makeQuery(id+"F2.boolean.opBoolean","SPLIT",FACE,{"disambiguationData":[TD([makeQuery(id+"F1.opExtrude","SWEPT_FACE",FACE,{"disambiguationData":[OSD([subQ6])]})])],"derivedFrom":makeQuery(id+"F1.opExtrude","CAP_FACE",FACE,{"disambiguationData":[OSD([subQ6,subQ8,subQ9,subQ7,subQ4,subQ3,subQ2,subQ1,subQ0,subQ5,subQ10,subQ11])],"isStart":true})});}
            var sketch = newSketch(context, id + "F16", { "sketchPlane" : qUnion([Q0])});
            skLineSegment(sketch, "E79", {"start": v(0, 74.25) * mm, "end": v(0, 104.25) * mm, "construction": true});
            skArc(sketch, "E80", {"start": v(15, 104.25) * mm, "mid": v(0, 119.25) * mm, "end": v(-15, 104.25) * mm});
            skLineSegment(sketch, "E81", {"start": v(15, 104.25) * mm, "end": v(15, 92.25) * mm});
            skLineSegment(sketch, "E82", {"start": v(-15, 104.25) * mm, "end": v(-15, 92.25) * mm});
            skLineSegment(sketch, "E83", {"start": v(-15, 92.25) * mm, "end": v(-33, 74.25) * mm});
            skLineSegment(sketch, "E84", {"start": v(15, 92.25) * mm, "end": v(33, 74.25) * mm});
            skCircle(sketch, "E85", {"center": v(0, 104.25) * mm, "radius": 6 * mm});
            skLineSegment(sketch, "E86", {"start": v(-74.25, 0) * mm, "end": v(74.25, 0) * mm, "construction": true});
            skLineSegment(sketch, "E87.MirrorCS", {"start": v(-15, -92.25) * mm, "end": v(-33, -74.25) * mm});
            skLineSegment(sketch, "E88.MirrorCS", {"start": v(15, -92.25) * mm, "end": v(33, -74.25) * mm});
            skCircle(sketch, "E89.MirrorC", {"center": v(0, -104.25) * mm, "radius": 6 * mm});
            skLineSegment(sketch, "E90.MirrorCS", {"start": v(-15, -104.25) * mm, "end": v(-15, -92.25) * mm});
            skLineSegment(sketch, "E91.MirrorCS", {"start": v(0, -74.25) * mm, "end": v(0, -104.25) * mm, "construction": true});
            skArc(sketch, "E92.MirrorCS", {"start": v(15, -104.25) * mm, "mid": v(0, -119.25) * mm, "end": v(-15, -104.25) * mm});
            skLineSegment(sketch, "E93.MirrorCS", {"start": v(15, -104.25) * mm, "end": v(15, -92.25) * mm});
            skSolve(sketch);
        }
        {
            var Q0;
            Q0=makeQuery(id+"F16.imprint","IMPRINT",FACE,{"disambiguationData":[TD([[makeQuery(id+"F16.imprint","IMPRINT",EDGE,{"derivedFrom":sQuery(id+"F16.wireOp",EDGE,"E80")}),1.0]])]});
            var Q1;
            Q1=makeQuery(id+"F16.imprint","IMPRINT",FACE,{"disambiguationData":[TD([[makeQuery(id+"F16.imprint","IMPRINT",EDGE,{"derivedFrom":makeQuery(id+"F1.opExtrude","CAP_EDGE",EDGE,{"disambiguationData":[OSD([sQuery(id+"F0.wireOp",EDGE,"E1.left")])],"isStart":true})}),-1.0]])]});
            var Q2;
            {var subQ1=sQuery(id+"F16.wireOp",EDGE,"E87.MirrorCS");Q2=makeQuery(id+"F16.imprint","IMPRINT",FACE,{"disambiguationData":[TD([[makeQuery(id+"F16.imprint","IMPRINT",EDGE,{"derivedFrom":subQ1}),-1.0]])]});}
            var Q3;
            Q3=makeQuery(id+"F2.opExtrude","CAP_FACE",FACE,{"disambiguationData":[OSD([sQuery(id+"F0.wireOp",EDGE,"E12"),sQuery(id+"F0.wireOp",EDGE,"E13"),sQuery(id+"F0.wireOp",EDGE,"E14"),sQuery(id+"F0.wireOp",EDGE,"E15"),sQuery(id+"F0.wireOp",EDGE,"E17.filletArc"),sQuery(id+"F0.wireOp",EDGE,"E18.filletArc"),sQuery(id+"F0.wireOp",EDGE,"E19.filletArc"),sQuery(id+"F0.wireOp",EDGE,"E20.filletArc"),sQuery(id+"F0.wireOp",EDGE,"E25.0"),sQuery(id+"F0.wireOp",EDGE,"E25.1"),sQuery(id+"F0.wireOp",EDGE,"E25.2"),sQuery(id+"F0.wireOp",EDGE,"E25.3"),sQuery(id+"F0.wireOp",EDGE,"E25.4"),sQuery(id+"F0.wireOp",EDGE,"E25.5"),sQuery(id+"F0.wireOp",EDGE,"E25.6"),sQuery(id+"F0.wireOp",EDGE,"E25.7")])],"isStart":false});
            extrude(context, id + "F17", {"entities" : qUnion([Q0, Q1, Q2]), "endBound" : BoundingType.UP_TO_SURFACE, "endBoundEntityFace" : qUnion([Q3]), "depth" : 25 * mm});
        }
    });
